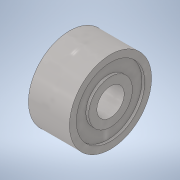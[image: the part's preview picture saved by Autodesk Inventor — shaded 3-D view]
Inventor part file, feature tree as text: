
AUTODESK INVENTOR PART (.ipt)
format: ipt  version: 2020.2 (Build 242310000, 310)  size: 155,648 bytes
history: native  units: mm
features: revolve x1, sketch x1
ambient origin geometry x8: Origin, YZ Plane, XZ Plane, XY Plane, X Axis, Y Axis, Z Axis, Center Point
bodies: Volumenkörper1 (feature_tree)
feature tree (2):
  revolve  "Umdrehung1"
  sketch  "Skizze1"  dims[d0=2.0mm d1=6.0mm d2=3.0mm d3=0.2mm d4=0.6mm d5=0.5mm d6=90.0deg]
